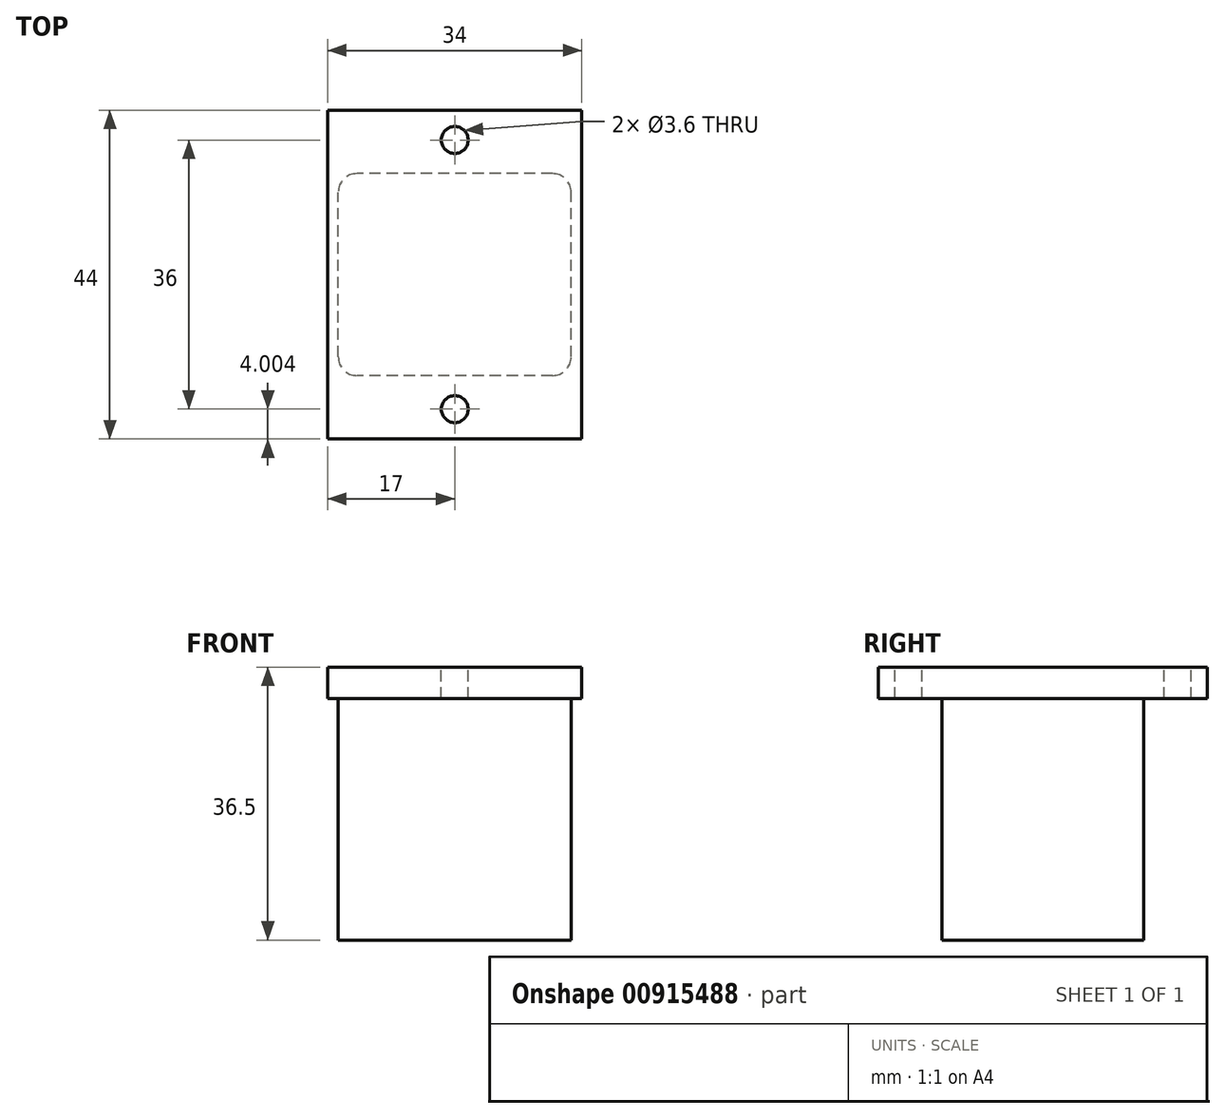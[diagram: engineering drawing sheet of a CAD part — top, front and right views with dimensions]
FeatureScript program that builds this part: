
annotation { "Feature Type Name" : "Feature", "Feature Type Description" : "" }
export const myFeature = defineFeature(function(context is Context, id is Id, definition is map)
    precondition{}
    {
        {
            var Q0;
            Q0=qCreatedBy(makeId("Top.planeOp"),FACE);
            var sketch = newSketch(context, id + "F0", { "sketchPlane" : qUnion([Q0])});
            skLineSegment(sketch, "E0.bottom", {"start": v(13.07, -13.5) * mm, "end": v(-13.07, -13.5) * mm});
            skLineSegment(sketch, "E0.top", {"start": v(13.07, 13.5) * mm, "end": v(-13.07, 13.5) * mm});
            skLineSegment(sketch, "E0.left", {"start": v(15.57, -11) * mm, "end": v(15.57, 11) * mm});
            skLineSegment(sketch, "E0.right", {"start": v(-15.58, -11) * mm, "end": v(-15.57, 11) * mm});
            skPoint(sketch, "E0.middle", {"position": v(0, 0) * mm});
            skPoint(sketch, "E1.visualSharp", {"position": v(15.57, 13.5) * mm});
            skArc(sketch, "E1.filletArc", {"start": v(15.57, 11) * mm, "mid": v(14.84, 12.77) * mm, "end": v(13.07, 13.5) * mm});
            skPoint(sketch, "E2.visualSharp", {"position": v(-15.57, 13.5) * mm});
            skArc(sketch, "E2.filletArc", {"start": v(-13.07, 13.5) * mm, "mid": v(-14.84, 12.77) * mm, "end": v(-15.57, 11) * mm});
            skPoint(sketch, "E3.visualSharp", {"position": v(-15.57, -13.5) * mm});
            skArc(sketch, "E3.filletArc", {"start": v(-15.58, -11) * mm, "mid": v(-14.84, -12.77) * mm, "end": v(-13.07, -13.5) * mm});
            skPoint(sketch, "E4.visualSharp", {"position": v(15.57, -13.5) * mm});
            skArc(sketch, "E4.filletArc", {"start": v(13.07, -13.5) * mm, "mid": v(14.84, -12.77) * mm, "end": v(15.57, -11) * mm});
            skSolve(sketch);
        }
        {
            var Q0;
            Q0 = qSketchRegion(id + "F0", true);
            extrude(context, id + "F1", {"entities" : qUnion([Q0]), "depth" : 32.3 * mm, "offsetDistance" : 25.4 * mm});
        }
        {
            var Q0;
            Q0=makeQuery(id+"F1.opExtrude","CAP_FACE",FACE,{"disambiguationData":[OSD([sQuery(id+"F0.wireOp",EDGE,"E0.bottom"),sQuery(id+"F0.wireOp",EDGE,"E0.top"),sQuery(id+"F0.wireOp",EDGE,"E0.left"),sQuery(id+"F0.wireOp",EDGE,"E0.right")])],"isStart":false});
            var sketch = newSketch(context, id + "F2", { "sketchPlane" : qUnion([Q0])});
            skLineSegment(sketch, "E5.bottom", {"start": v(17, -22) * mm, "end": v(-17, -22) * mm});
            skLineSegment(sketch, "E5.top", {"start": v(17, 22) * mm, "end": v(-17, 22) * mm});
            skLineSegment(sketch, "E5.left", {"start": v(17, -22) * mm, "end": v(17, 22) * mm});
            skLineSegment(sketch, "E5.right", {"start": v(-17, -22) * mm, "end": v(-17, 22) * mm});
            skPoint(sketch, "E5.middle", {"position": v(0, 0) * mm});
            skSolve(sketch);
        }
        {
            var Q0;
            Q0=makeQuery(id+"F2.imprint","IMPRINT",FACE,{"disambiguationData":[TD([[makeQuery(id+"F2.imprint","IMPRINT",EDGE,{"derivedFrom":sQuery(id+"F2.wireOp",EDGE,"E5.bottom")}),-1.0]])]});
            var Q1;
            Q1=makeQuery(id+"F2.imprint","IMPRINT",FACE,{"disambiguationData":[TD([[makeQuery(id+"F2.imprint","IMPRINT",EDGE,{"derivedFrom":makeQuery(id+"F1.opExtrude","CAP_EDGE",EDGE,{"disambiguationData":[OSD([sQuery(id+"F0.wireOp",EDGE,"E0.bottom")])],"isStart":false})}),-1.0]])]});
            extrude(context, id + "F3", {"entities" : qUnion([Q0, Q1]), "operationType" : NewBodyOperationType.ADD, "depth" : 4.2 * mm, "offsetDistance" : 25.4 * mm});
        }
        {
            var Q0;
            Q0=makeQuery(id+"F3.opExtrude","CAP_FACE",FACE,{"disambiguationData":[OSD([sQuery(id+"F2.wireOp",EDGE,"E5.bottom"),sQuery(id+"F2.wireOp",EDGE,"E5.top"),sQuery(id+"F2.wireOp",EDGE,"E5.left"),sQuery(id+"F2.wireOp",EDGE,"E5.right")])],"isStart":false});
            var sketch = newSketch(context, id + "F4", { "sketchPlane" : qUnion([Q0])});
            skLineSegment(sketch, "E6", {"start": v(17, 18) * mm, "end": v(-17, 18) * mm, "construction": true});
            skLineSegment(sketch, "E7", {"start": v(17, -18) * mm, "end": v(-17, -18) * mm, "construction": true});
            skLineSegment(sketch, "E8", {"start": v(0, 22) * mm, "end": v(0, -22) * mm, "construction": true});
            skCircle(sketch, "E9", {"center": v(0, 18) * mm, "radius": 1.8 * mm});
            skCircle(sketch, "E10", {"center": v(0, -18) * mm, "radius": 1.8 * mm});
            skSolve(sketch);
        }
        {
            var Q0;
            Q0=makeQuery(id+"F4.imprint","IMPRINT",FACE,{"disambiguationData":[TD([[makeQuery(id+"F4.imprint","IMPRINT",EDGE,{"derivedFrom":sQuery(id+"F4.wireOp",EDGE,"E9")}),1.0]])]});
            var Q1;
            Q1=makeQuery(id+"F4.imprint","IMPRINT",FACE,{"disambiguationData":[TD([[makeQuery(id+"F4.imprint","IMPRINT",EDGE,{"derivedFrom":sQuery(id+"F4.wireOp",EDGE,"E10")}),1.0]])]});
            extrude(context, id + "F5", {"entities" : qUnion([Q0, Q1]), "operationType" : NewBodyOperationType.REMOVE, "oppositeDirection" : true, "depth" : 25.4 * mm, "offsetDistance" : 25.4 * mm});
        }
    });
